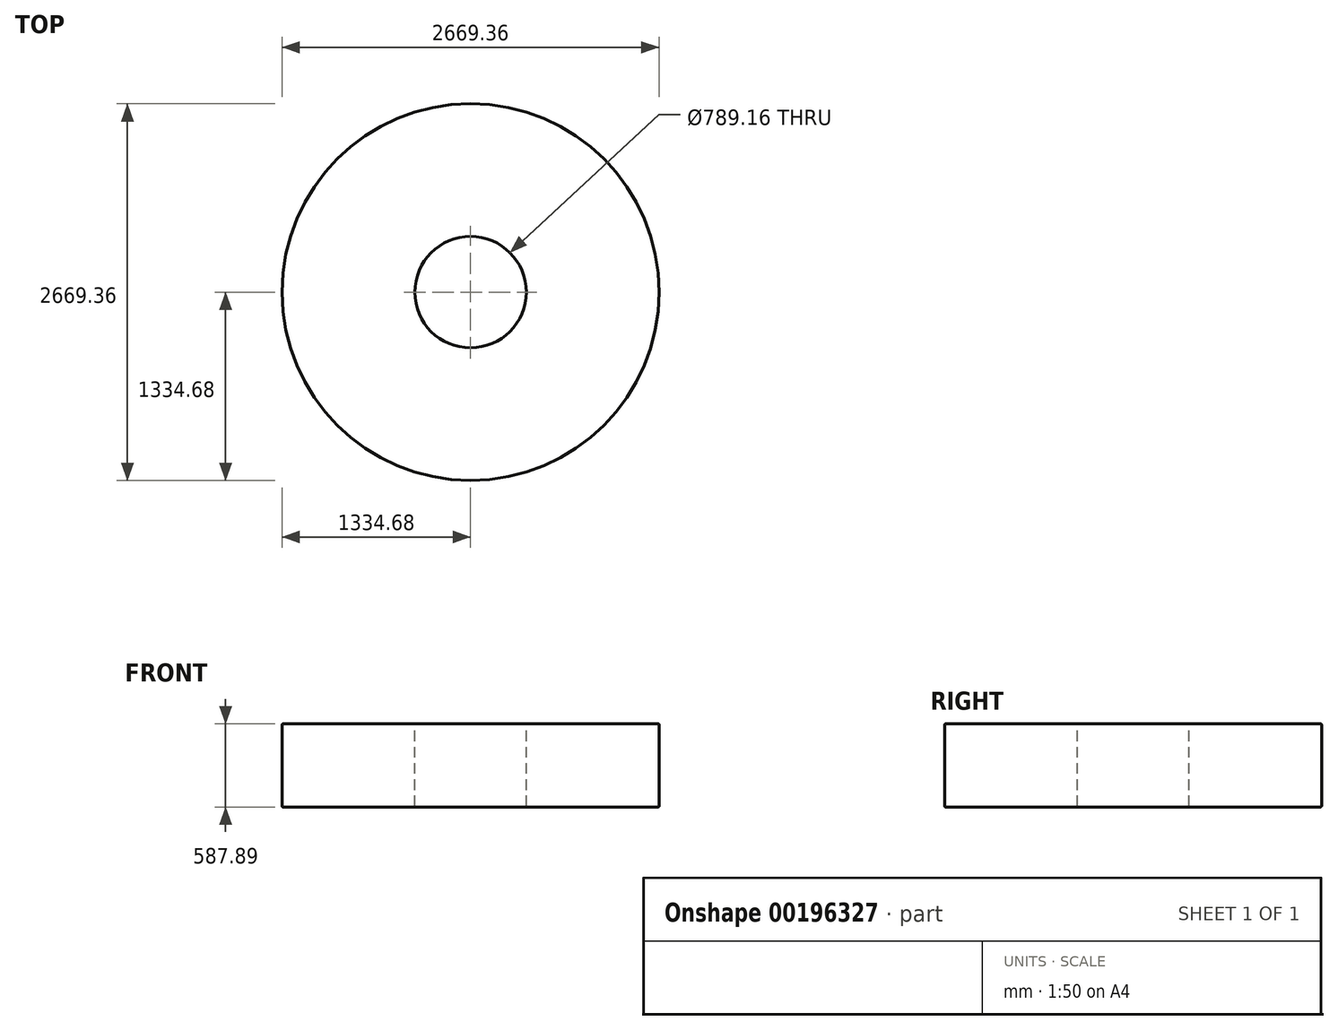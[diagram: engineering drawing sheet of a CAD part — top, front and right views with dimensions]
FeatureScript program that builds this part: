
annotation { "Feature Type Name" : "Feature", "Feature Type Description" : "" }
export const myFeature = defineFeature(function(context is Context, id is Id, definition is map)
    precondition{}
    {
        {
            var Q0;
            Q0=qCreatedBy(makeId("Front.planeOp"),FACE);
            var sketch = newSketch(context, id + "F0", { "sketchPlane" : qUnion([Q0])});
            skLineSegment(sketch, "E0.bottom", {"start": v(-797.1, 395.9) * mm, "end": v(143, 395.9) * mm});
            skLineSegment(sketch, "E0.top", {"start": v(-797.1, -192) * mm, "end": v(143, -192) * mm});
            skLineSegment(sketch, "E0.left", {"start": v(-797.1, 395.9) * mm, "end": v(-797.1, -192) * mm});
            skLineSegment(sketch, "E0.right", {"start": v(143, 395.9) * mm, "end": v(143, -192) * mm});
            skLineSegment(sketch, "E1", {"start": v(537.58, 356.18) * mm, "end": v(537.58, -229.07) * mm});
            skSolve(sketch);
        }
        {
            var Q0;
            Q0=makeQuery(id+"F0.imprint","IMPRINT",FACE,{"disambiguationData":[TD([[makeQuery(id+"F0.imprint","IMPRINT",EDGE,{"derivedFrom":sQuery(id+"F0.wireOp",EDGE,"E0.bottom")}),-1.0]])]});
            var Q1;
            Q1=sQuery(id+"F0.wireOp",EDGE,"E1");
            revolve(context, id + "F1", {"entities" : qUnion([Q0]), "axis" : qUnion([Q1]), "revolveType" : RevolveType.FULL});
        }
        {
            var Q0;
            Q0=makeQuery(id+"F1.opRevolve","SWEPT_FACE",FACE,{"disambiguationData":[OSD([sQuery(id+"F0.wireOp",EDGE,"E0.top")])]});
            var Q1;
            Q1=makeQuery(id+"F1.opRevolve","SWEPT_EDGE",EDGE,{"disambiguationData":[OSD([sQuery(id+"F0.wireOp",EDGE,"E0.top"),sQuery(id+"F0.wireOp",EDGE,"E0.left")])]});
            var Q2;
            Q2=makeQuery(id+"F1.opRevolve","SWEPT_EDGE",EDGE,{"disambiguationData":[OSD([sQuery(id+"F0.wireOp",EDGE,"E0.bottom"),sQuery(id+"F0.wireOp",EDGE,"E0.left")])]});
            var Q3;
            Q3=makeQuery(id+"F1.opRevolve","SWEPT_FACE",FACE,{"disambiguationData":[OSD([sQuery(id+"F0.wireOp",EDGE,"E0.left")])]});
            var Q4;
            Q4=makeQuery(id+"F1.opRevolve","SWEPT_EDGE",EDGE,{"disambiguationData":[OSD([sQuery(id+"F0.wireOp",EDGE,"E0.bottom"),sQuery(id+"F0.wireOp",EDGE,"E0.right")])]});
            fillet(context, id + "F2", {"entities" : qUnion([Q0, Q1, Q2, Q3, Q4]), "radius" : 5.08 * mm, "tangentPropagation" : true, "allowEdgeOverflow" : false});
        }
    });
